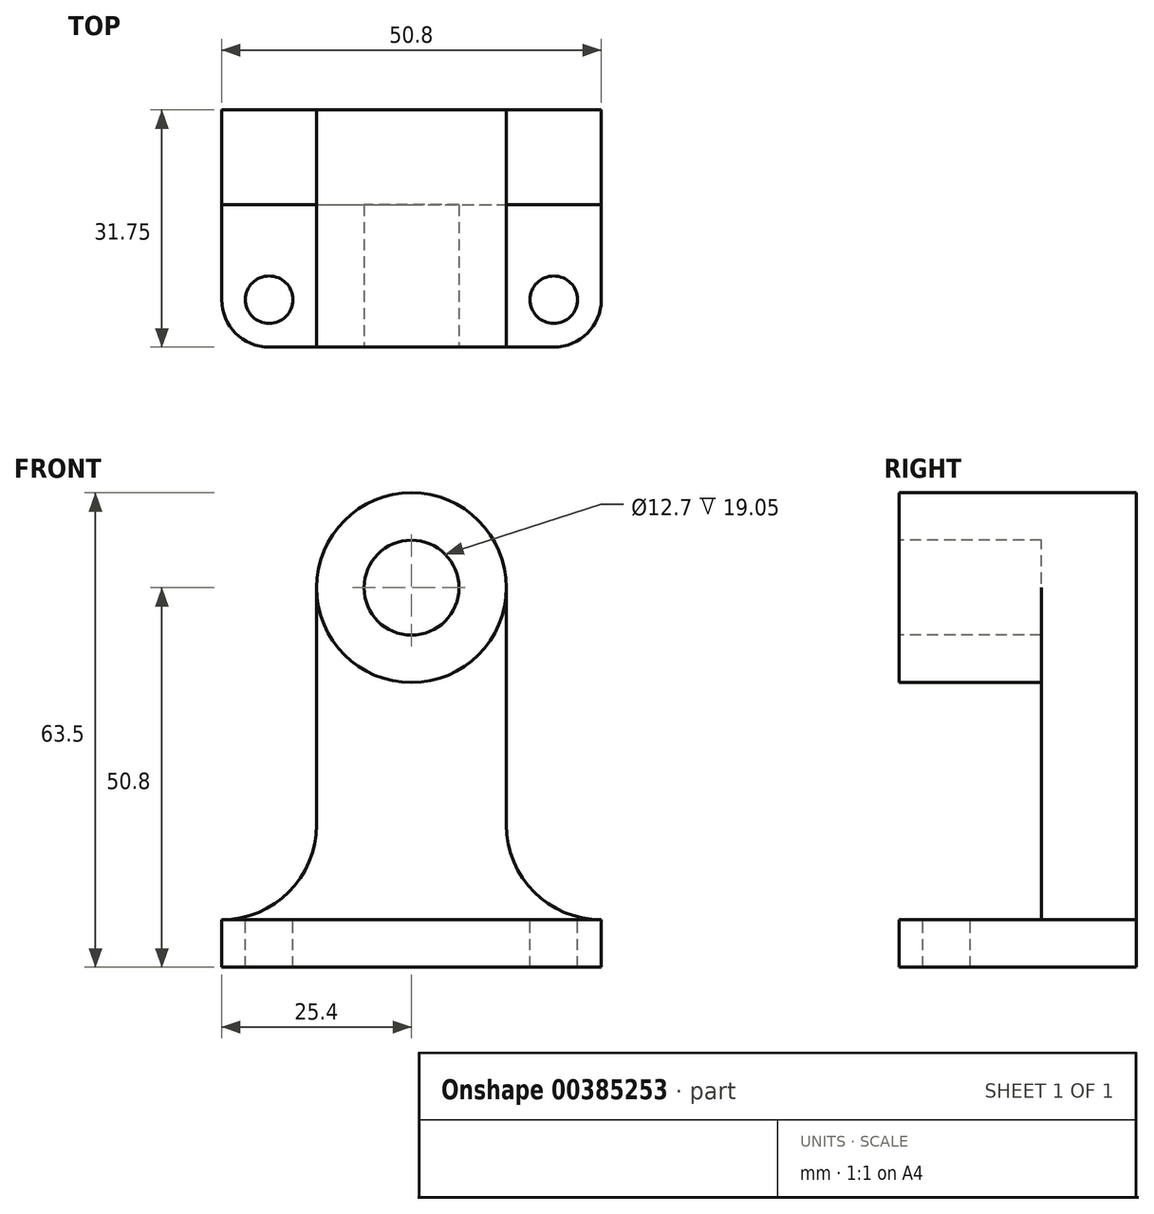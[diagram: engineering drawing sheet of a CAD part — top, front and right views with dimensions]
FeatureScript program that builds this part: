
annotation { "Feature Type Name" : "Feature", "Feature Type Description" : "" }
export const myFeature = defineFeature(function(context is Context, id is Id, definition is map)
    precondition{}
    {
        {
            var Q0;
            Q0=qCreatedBy(makeId("Front.planeOp"),FACE);
            var sketch = newSketch(context, id + "F0", { "sketchPlane" : qUnion([Q0])});
            skLineSegment(sketch, "E0.bottom", {"start": v(0, 0) * mm, "end": v(50.8, 0) * mm});
            skLineSegment(sketch, "E0.top", {"start": v(0, 63.5) * mm, "end": v(50.8, 63.5) * mm});
            skLineSegment(sketch, "E0.left", {"start": v(0, 0) * mm, "end": v(0, 63.5) * mm});
            skLineSegment(sketch, "E0.right", {"start": v(50.8, 0) * mm, "end": v(50.8, 63.5) * mm});
            skSolve(sketch);
        }
        {
            var Q0;
            Q0=qSketchRegion(id+"F0",true);
            extrude(context, id + "F1", {"entities" : qUnion([Q0]), "depth" : 31.75 * mm});
        }
        {
            var Q0;
            Q0=makeQuery(id+"F1.opExtrude","CAP_FACE",FACE,{"disambiguationData":[OSD([sQuery(id+"F0.wireOp",EDGE,"E0.bottom"),sQuery(id+"F0.wireOp",EDGE,"E0.top"),sQuery(id+"F0.wireOp",EDGE,"E0.left"),sQuery(id+"F0.wireOp",EDGE,"E0.right")])],"isStart":false});
            var sketch = newSketch(context, id + "F2", { "sketchPlane" : qUnion([Q0])});
            skLineSegment(sketch, "E1", {"start": v(0, 6.35) * mm, "end": v(50.8, 6.35) * mm});
            skArc(sketch, "E2", {"start": v(0, 6.35) * mm, "mid": v(8.98, 10.07) * mm, "end": v(12.7, 19.05) * mm});
            skArc(sketch, "E3", {"start": v(38.1, 19.05) * mm, "mid": v(41.82, 10.07) * mm, "end": v(50.8, 6.35) * mm});
            skLineSegment(sketch, "E4", {"start": v(12.7, 50.8) * mm, "end": v(12.7, 19.05) * mm});
            skLineSegment(sketch, "E5", {"start": v(38.1, 19.05) * mm, "end": v(38.1, 50.8) * mm});
            skArc(sketch, "E6", {"start": v(38.1, 50.8) * mm, "mid": v(25.4, 63.5) * mm, "end": v(12.7, 50.8) * mm});
            skSolve(sketch);
        }
        {
            var Q0;
            {var subQ6=sQuery(id+"F2.wireOp",EDGE,"E2");Q0=makeQuery(id+"F2.imprint","IMPRINT",FACE,{"disambiguationData":[TD([[makeQuery(id+"F2.imprint","IMPRINT",EDGE,{"derivedFrom":subQ6}),1.0]])]});}
            var Q1;
            {var subQ6=sQuery(id+"F2.wireOp",EDGE,"E3");Q1=makeQuery(id+"F2.imprint","IMPRINT",FACE,{"disambiguationData":[TD([[makeQuery(id+"F2.imprint","IMPRINT",EDGE,{"derivedFrom":subQ6}),1.0]])]});}
            extrude(context, id + "F3", {"entities" : qUnion([Q0, Q1]), "operationType" : NewBodyOperationType.REMOVE, "oppositeDirection" : true, "depth" : 31.75 * mm});
        }
        {
            var Q0;
            Q0=makeQuery(id+"F1.opExtrude","CAP_FACE",FACE,{"disambiguationData":[OSD([sQuery(id+"F0.wireOp",EDGE,"E0.bottom"),sQuery(id+"F0.wireOp",EDGE,"E0.top"),sQuery(id+"F0.wireOp",EDGE,"E0.left"),sQuery(id+"F0.wireOp",EDGE,"E0.right")])],"isStart":false});
            var sketch = newSketch(context, id + "F4", { "sketchPlane" : qUnion([Q0])});
            skCircle(sketch, "E7", {"center": v(25.4, 50.8) * mm, "radius": 6.35 * mm});
            skCircle(sketch, "E8", {"center": v(25.4, 50.8) * mm, "radius": 12.7 * mm});
            skLineSegment(sketch, "E9", {"start": v(0, 6.35) * mm, "end": v(50.8, 6.35) * mm});
            skSolve(sketch);
        }
        {
            var Q0;
            Q0=makeQuery(id+"F4.imprint","IMPRINT",FACE,{"disambiguationData":[TD([[makeQuery(id+"F4.imprint","IMPRINT",EDGE,{"derivedFrom":sQuery(id+"F4.wireOp",EDGE,"E9")}),1.0]])]});
            var Q1;
            Q1=makeQuery(id+"F4.imprint","IMPRINT",FACE,{"disambiguationData":[TD([[makeQuery(id+"F4.imprint","IMPRINT",EDGE,{"derivedFrom":sQuery(id+"F4.wireOp",EDGE,"E7")}),1.0]])]});
            extrude(context, id + "F5", {"entities" : qUnion([Q0, Q1]), "operationType" : NewBodyOperationType.REMOVE, "oppositeDirection" : true, "depth" : 19.05 * mm});
        }
        {
            var Q0;
            Q0=makeQuery(id+"F5.boolean.opBoolean","COPY",FACE,{"derivedFrom":makeQuery(id+"F5.opExtrude","SWEPT_FACE",FACE,{"disambiguationData":[OSD([sQuery(id+"F4.wireOp",EDGE,"E9")])]})});
            var sketch = newSketch(context, id + "F6", { "sketchPlane" : qUnion([Q0])});
            skCircle(sketch, "E10", {"center": v(6.35, -25.4) * mm, "radius": 3.18 * mm});
            skCircle(sketch, "E11", {"center": v(44.45, -25.4) * mm, "radius": 3.17 * mm});
            skArc(sketch, "E12", {"start": v(0, -25.4) * mm, "mid": v(1.86, -29.9) * mm, "end": v(6.35, -31.75) * mm});
            skArc(sketch, "E13", {"start": v(44.45, -31.75) * mm, "mid": v(48.94, -29.9) * mm, "end": v(50.8, -25.4) * mm});
            skSolve(sketch);
        }
        {
            var Q0;
            Q0=makeQuery(id+"F6.imprint","IMPRINT",FACE,{"disambiguationData":[TD([[makeQuery(id+"F6.imprint","IMPRINT",EDGE,{"derivedFrom":sQuery(id+"F6.wireOp",EDGE,"E10")}),1.0]])]});
            var Q1;
            {var subQ0=sQuery(id+"F6.wireOp",EDGE,"E12");Q1=makeQuery(id+"F6.imprint","IMPRINT",FACE,{"disambiguationData":[TD([[makeQuery(id+"F6.imprint","IMPRINT",EDGE,{"derivedFrom":subQ0}),-1.0]])]});}
            var Q2;
            Q2=makeQuery(id+"F6.imprint","IMPRINT",FACE,{"disambiguationData":[TD([[makeQuery(id+"F6.imprint","IMPRINT",EDGE,{"derivedFrom":sQuery(id+"F6.wireOp",EDGE,"E11")}),1.0]])]});
            var Q3;
            {var subQ0=sQuery(id+"F6.wireOp",EDGE,"E13");Q3=makeQuery(id+"F6.imprint","IMPRINT",FACE,{"disambiguationData":[TD([[makeQuery(id+"F6.imprint","IMPRINT",EDGE,{"derivedFrom":subQ0}),-1.0]])]});}
            extrude(context, id + "F7", {"entities" : qUnion([Q0, Q1, Q2, Q3]), "operationType" : NewBodyOperationType.REMOVE, "oppositeDirection" : true, "depth" : 25.4 * mm});
        }
    });
